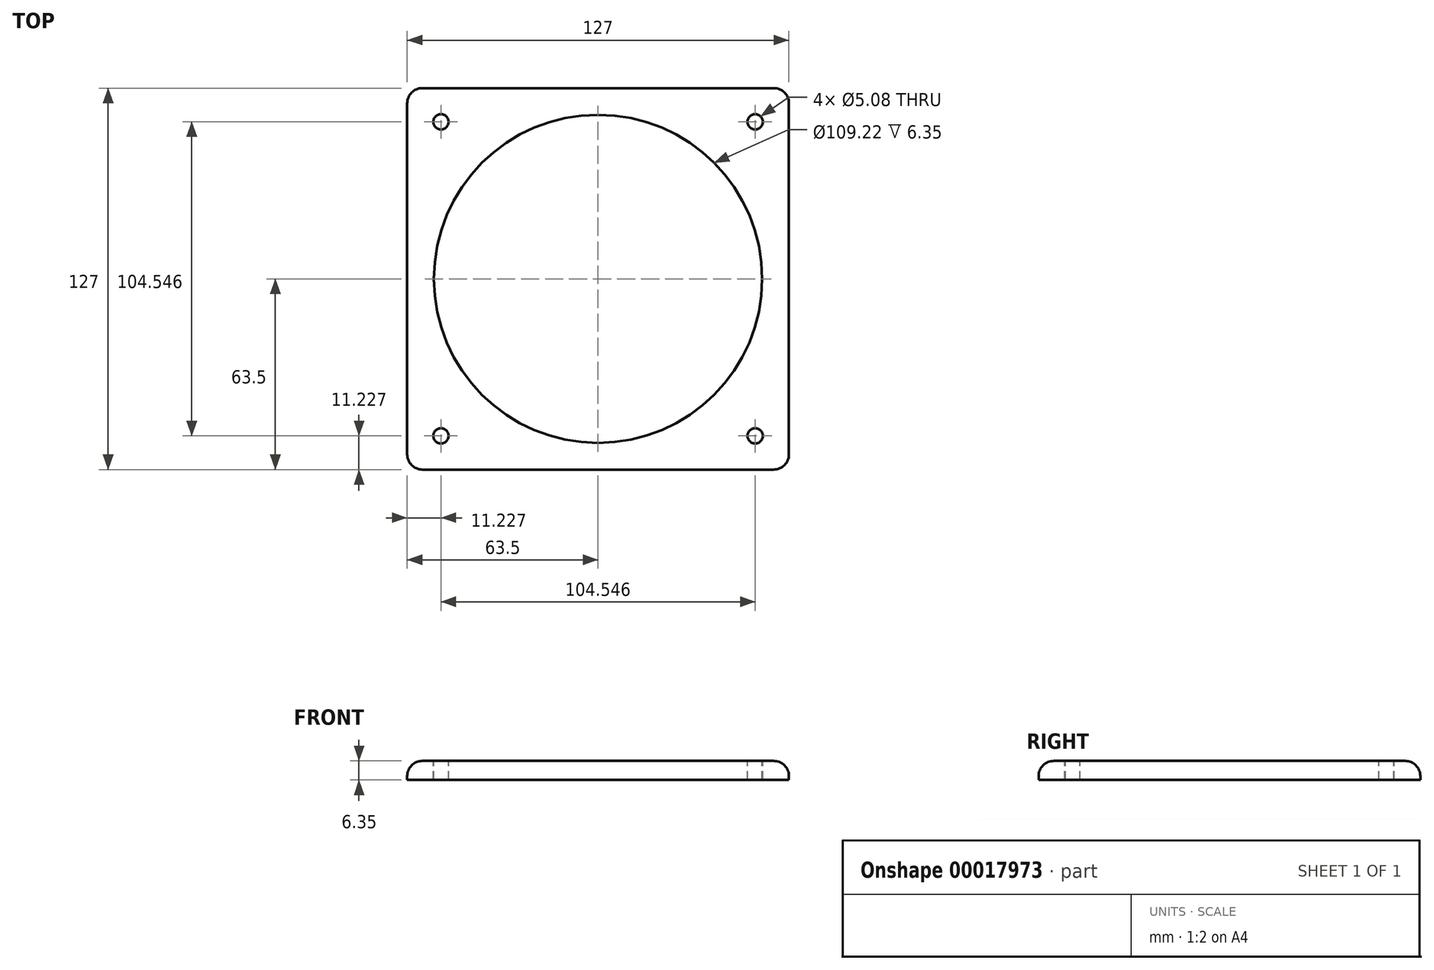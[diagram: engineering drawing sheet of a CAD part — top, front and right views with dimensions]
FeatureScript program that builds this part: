
annotation { "Feature Type Name" : "Feature", "Feature Type Description" : "" }
export const myFeature = defineFeature(function(context is Context, id is Id, definition is map)
    precondition{}
    {
        {
            var Q0;
            Q0=qCreatedBy(makeId("Top.planeOp"),FACE);
            var sketch = newSketch(context, id + "F0", { "sketchPlane" : qUnion([Q0])});
            skLineSegment(sketch, "E0.bottom", {"start": v(63.5, -63.5) * mm, "end": v(-63.5, -63.5) * mm});
            skLineSegment(sketch, "E0.top", {"start": v(63.5, 63.5) * mm, "end": v(-63.5, 63.5) * mm});
            skLineSegment(sketch, "E0.left", {"start": v(63.5, -63.5) * mm, "end": v(63.5, 63.5) * mm});
            skLineSegment(sketch, "E0.right", {"start": v(-63.5, -63.5) * mm, "end": v(-63.5, 63.5) * mm});
            skPoint(sketch, "E0.middle", {"position": v(0, 0) * mm});
            skSolve(sketch);
        }
        {
            var Q0;
            Q0=makeQuery(id+"F0.imprint","IMPRINT",FACE,{"disambiguationData":[TD([[makeQuery(id+"F0.imprint","IMPRINT",EDGE,{"derivedFrom":sQuery(id+"F0.wireOp",EDGE,"E0.bottom")}),-1.0]])]});
            extrude(context, id + "F1", {"entities" : qUnion([Q0]), "depth" : 6.35 * mm});
        }
        {
            var Q0;
            Q0=makeQuery(id+"F1.opExtrude","CAP_FACE",FACE,{"disambiguationData":[OSD([sQuery(id+"F0.wireOp",EDGE,"E0.bottom"),sQuery(id+"F0.wireOp",EDGE,"E0.top"),sQuery(id+"F0.wireOp",EDGE,"E0.left"),sQuery(id+"F0.wireOp",EDGE,"E0.right")])],"isStart":false});
            var sketch = newSketch(context, id + "F2", { "sketchPlane" : qUnion([Q0])});
            skCircle(sketch, "E1", {"center": v(0, 0) * mm, "radius": 54.6 * mm});
            skSolve(sketch);
        }
        {
            var Q0;
            Q0=makeQuery(id+"F2.imprint","IMPRINT",FACE,{"disambiguationData":[TD([[makeQuery(id+"F2.imprint","IMPRINT",EDGE,{"derivedFrom":sQuery(id+"F2.wireOp",EDGE,"E1")}),1.0]])]});
            extrude(context, id + "F3", {"entities" : qUnion([Q0]), "operationType" : NewBodyOperationType.REMOVE, "oppositeDirection" : true, "depth" : 38.1 * mm});
        }
        {
            var Q0;
            Q0=makeQuery(id+"F1.opExtrude","SWEPT_EDGE",EDGE,{"disambiguationData":[OSD([sQuery(id+"F0.wireOp",EDGE,"E0.top"),sQuery(id+"F0.wireOp",EDGE,"E0.left")])]});
            var Q1;
            Q1=makeQuery(id+"F1.opExtrude","SWEPT_EDGE",EDGE,{"disambiguationData":[OSD([sQuery(id+"F0.wireOp",EDGE,"E0.top"),sQuery(id+"F0.wireOp",EDGE,"E0.right")])]});
            var Q2;
            Q2=makeQuery(id+"F1.opExtrude","SWEPT_EDGE",EDGE,{"disambiguationData":[OSD([sQuery(id+"F0.wireOp",EDGE,"E0.bottom"),sQuery(id+"F0.wireOp",EDGE,"E0.left")])]});
            var Q3;
            Q3=makeQuery(id+"F1.opExtrude","SWEPT_EDGE",EDGE,{"disambiguationData":[OSD([sQuery(id+"F0.wireOp",EDGE,"E0.bottom"),sQuery(id+"F0.wireOp",EDGE,"E0.right")])]});
            fillet(context, id + "F4", {"entities" : qUnion([Q0, Q1, Q2, Q3]), "radius" : 5.08 * mm, "tangentPropagation" : true, "allowEdgeOverflow" : false});
        }
        {
            var Q0;
            Q0=makeQuery(id+"F1.opExtrude","CAP_FACE",FACE,{"disambiguationData":[OSD([sQuery(id+"F0.wireOp",EDGE,"E0.bottom"),sQuery(id+"F0.wireOp",EDGE,"E0.top"),sQuery(id+"F0.wireOp",EDGE,"E0.left"),sQuery(id+"F0.wireOp",EDGE,"E0.right")])],"isStart":false});
            var sketch = newSketch(context, id + "F5", { "sketchPlane" : qUnion([Q0])});
            skCircle(sketch, "E2", {"center": v(-52.27, 52.27) * mm, "radius": 2.54 * mm});
            skCircle(sketch, "E3", {"center": v(52.27, 52.27) * mm, "radius": 2.54 * mm});
            skCircle(sketch, "E4", {"center": v(52.27, -52.27) * mm, "radius": 2.54 * mm});
            skCircle(sketch, "E5", {"center": v(-52.27, -52.27) * mm, "radius": 2.54 * mm});
            skSolve(sketch);
        }
        {
            var Q0;
            Q0=makeQuery(id+"F5.imprint","IMPRINT",FACE,{"disambiguationData":[TD([[makeQuery(id+"F5.imprint","IMPRINT",EDGE,{"derivedFrom":sQuery(id+"F5.wireOp",EDGE,"E2")}),1.0]])]});
            var Q1;
            Q1=makeQuery(id+"F5.imprint","IMPRINT",FACE,{"disambiguationData":[TD([[makeQuery(id+"F5.imprint","IMPRINT",EDGE,{"derivedFrom":sQuery(id+"F5.wireOp",EDGE,"E3")}),1.0]])]});
            var Q2;
            Q2=makeQuery(id+"F5.imprint","IMPRINT",FACE,{"disambiguationData":[TD([[makeQuery(id+"F5.imprint","IMPRINT",EDGE,{"derivedFrom":sQuery(id+"F5.wireOp",EDGE,"E4")}),1.0]])]});
            var Q3;
            Q3=makeQuery(id+"F5.imprint","IMPRINT",FACE,{"disambiguationData":[TD([[makeQuery(id+"F5.imprint","IMPRINT",EDGE,{"derivedFrom":sQuery(id+"F5.wireOp",EDGE,"E5")}),1.0]])]});
            extrude(context, id + "F6", {"entities" : qUnion([Q0, Q1, Q2, Q3]), "operationType" : NewBodyOperationType.REMOVE, "endBound" : BoundingType.THROUGH_ALL, "oppositeDirection" : true, "depth" : 25.4 * mm});
        }
        {
            var Q0;
            Q0=makeQuery(id+"F1.opExtrude","CAP_EDGE",EDGE,{"disambiguationData":[OSD([sQuery(id+"F0.wireOp",EDGE,"E0.bottom")])],"isStart":false});
            fillet(context, id + "F7", {"entities" : qUnion([Q0]), "radius" : 5.08 * mm, "tangentPropagation" : true, "allowEdgeOverflow" : false});
        }
    });
